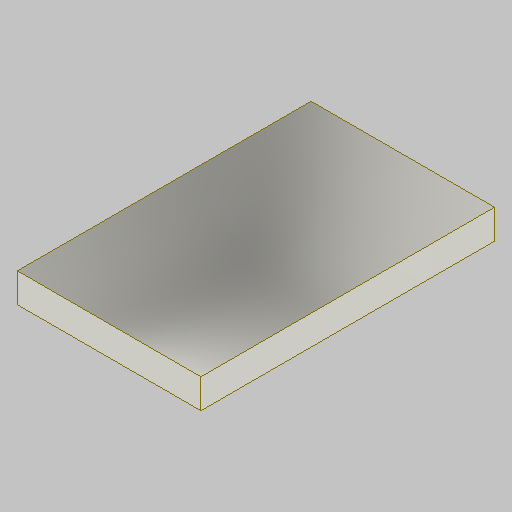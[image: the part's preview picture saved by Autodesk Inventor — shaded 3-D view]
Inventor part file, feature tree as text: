
AUTODESK INVENTOR PART (.ipt)
format: ipt  version: 2025.2 (Build 292293000, 293)  size: 206,848 bytes
history: native  units: in
note: dims shown in document units (in); Inventor stores cm internally (conversion verified against a paired STEP export)
features: extrude x1, sketch x1
ambient origin geometry x8: Origin, YZ Plane, XZ Plane, XY Plane, X Axis, Y Axis, Z Axis, Center Point
bodies: Solid1 (feature_tree)
feature tree (2):
  extrude  "Extrusion1"  Depth=1.5748in
  sketch  "Sketch1"  dims[d0=0.9843in d1=1.5748in d2=0.1575in d3=0.0in]
